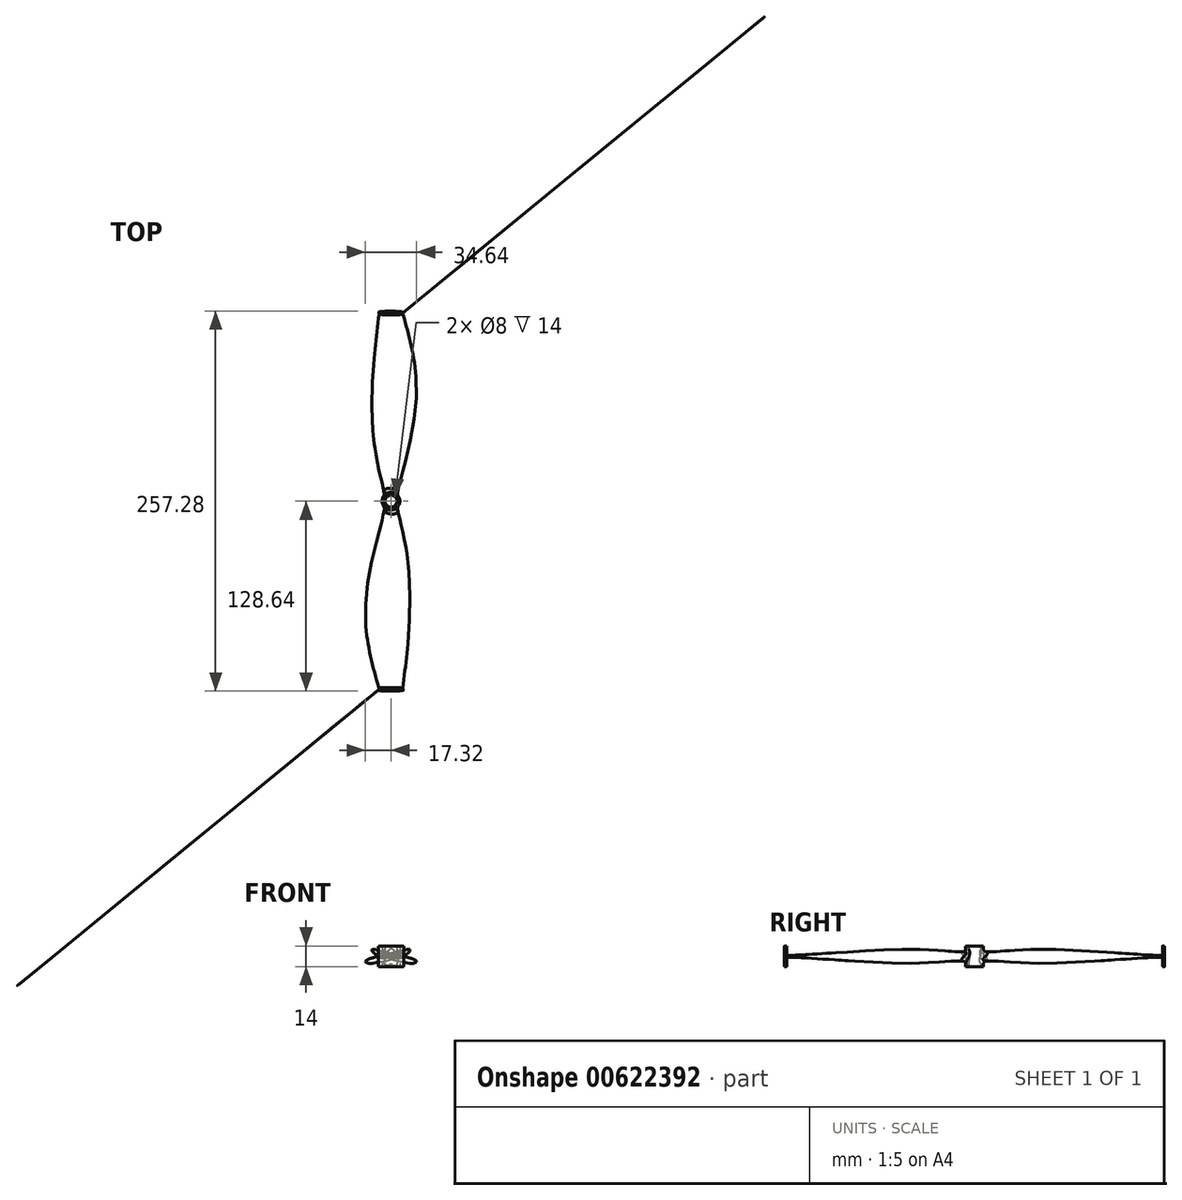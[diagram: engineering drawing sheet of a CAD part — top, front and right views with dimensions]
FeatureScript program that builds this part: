
annotation { "Feature Type Name" : "Feature", "Feature Type Description" : "" }
export const myFeature = defineFeature(function(context is Context, id is Id, definition is map)
    precondition{}
    {
        {
            var Q0;
            Q0=qCreatedBy(makeId("Top.planeOp"),FACE);
            var sketch = newSketch(context, id + "F0", { "sketchPlane" : qUnion([Q0])});
            skCircle(sketch, "E0", {"center": v(0, 0) * mm, "radius": 6 * mm});
            skCircle(sketch, "E1.0", {"center": v(0, 0) * mm, "radius": 4 * mm});
            skSolve(sketch);
        }
        {
            var Q0;
            Q0=qCreatedBy(makeId("Front.planeOp"),FACE);
            cPlane(context, id + "F1", {"entities" : qUnion([Q0]), "cplaneType" : CPlaneType.OFFSET, "offset" : 2 * mm, "width" : 150 * mm, "height" : 150 * mm});
        }
        {
            var Q0;
            Q0=qCreatedBy(makeId("Front.planeOp"),FACE);
            cPlane(context, id + "F2", {"entities" : qUnion([Q0]), "cplaneType" : CPlaneType.OFFSET, "offset" : 18 * mm, "width" : 150 * mm, "height" : 150 * mm});
        }
        {
            var Q0;
            Q0=qCreatedBy(makeId("Front.planeOp"),FACE);
            cPlane(context, id + "F3", {"entities" : qUnion([Q0]), "cplaneType" : CPlaneType.OFFSET, "offset" : 84 * mm, "width" : 150 * mm, "height" : 150 * mm});
        }
        {
            var Q0;
            Q0=qCreatedBy(makeId("Front.planeOp"),FACE);
            cPlane(context, id + "F4", {"entities" : qUnion([Q0]), "cplaneType" : CPlaneType.OFFSET, "offset" : 128 * mm, "width" : 150 * mm, "height" : 150 * mm});
        }
        {
            var Q0;
            Q0=qCreatedBy(id+"F1.planeOp",FACE);
            var sketch = newSketch(context, id + "F5", { "sketchPlane" : qUnion([Q0])});
            skLineSegment(sketch, "E2", {"start": v(-9.97, 0) * mm, "end": v(8.52, 0) * mm, "construction": true});
            skLineSegment(sketch, "E3", {"start": v(5.45, 4.57) * mm, "end": v(0, 0) * mm, "construction": true});
            skLineSegment(sketch, "E4", {"start": v(0, 0) * mm, "end": v(4.94, -5.88) * mm, "construction": true});
            skEllipse(sketch, "E5", {"center": v(0, 0) * mm, "majorRadius": 5 * mm, "minorRadius": 2 * mm, "majorAxis": v(0.76, 0.64)});
            skSolve(sketch);
        }
        {
            var Q0;
            Q0=qCreatedBy(id+"F2.planeOp",FACE);
            var sketch = newSketch(context, id + "F6", { "sketchPlane" : qUnion([Q0])});
            skLineSegment(sketch, "E6", {"start": v(-11.2, 0) * mm, "end": v(9.29, 0) * mm, "construction": true});
            skLineSegment(sketch, "E7", {"start": v(9.29, 0) * mm, "end": v(0, 0) * mm, "construction": true});
            skLineSegment(sketch, "E8", {"start": v(0, 0) * mm, "end": v(2.83, -6.16) * mm, "construction": true});
            skLineSegment(sketch, "E9", {"start": v(0, 0) * mm, "end": v(8.55, 3.92) * mm, "construction": true});
            skEllipse(sketch, "E10", {"center": v(0, 0) * mm, "majorRadius": 8 * mm, "minorRadius": 1.43 * mm, "majorAxis": v(0.92, 0.4)});
            skSolve(sketch);
        }
        {
            var Q0;
            Q0=qCreatedBy(id+"F3.planeOp",FACE);
            var sketch = newSketch(context, id + "F7", { "sketchPlane" : qUnion([Q0])});
            skEllipse(sketch, "E11", {"center": v(-2.33, 0) * mm, "majorRadius": 15 * mm, "minorRadius": 0.74 * mm, "majorAxis": v(0.98, 0.2)});
            skSolve(sketch);
        }
        {
            var Q0;
            Q0=qCreatedBy(id+"F4.planeOp",FACE);
            var sketch = newSketch(context, id + "F8", { "sketchPlane" : qUnion([Q0])});
            skEllipse(sketch, "E12", {"center": v(0, 0) * mm, "majorRadius": 7.81 * mm, "minorRadius": 0.53 * mm, "majorAxis": v(1, 0)});
            skSolve(sketch);
        }
        {
            var Q0;
            Q0=qCreatedBy(makeId("Front.planeOp"),FACE);
            var sketch = newSketch(context, id + "F9", { "sketchPlane" : qUnion([Q0])});
            skLineSegment(sketch, "E13", {"start": v(0, -14) * mm, "end": v(0, 19.94) * mm, "construction": true});
            skLineSegment(sketch, "E14", {"start": v(23.62, 0) * mm, "end": v(-25.85, 0) * mm, "construction": true});
            skSolve(sketch);
        }
        {
            var Q0;
            Q0=makeQuery(id+"F0.imprint","IMPRINT",FACE,{"disambiguationData":[TD([[makeQuery(id+"F0.imprint","IMPRINT",EDGE,{"derivedFrom":sQuery(id+"F0.wireOp",EDGE,"E0")}),1.0]])]});
            var Q1;
            Q1=makeQuery(id+"F0.imprint","IMPRINT",FACE,{"disambiguationData":[TD([[makeQuery(id+"F0.imprint","IMPRINT",EDGE,{"derivedFrom":sQuery(id+"F0.wireOp",EDGE,"E1.0")}),1.0]])]});
            extrude(context, id + "F10", {"entities" : qUnion([Q0, Q1]), "depth" : 14 * mm, "offsetDistance" : 25 * mm, "symmetric" : true});
        }
        {
            var Q1;
            Q1 = qSketchRegion(id + "F5", true);
            var Q2;
            Q2 = qSketchRegion(id + "F6", true);
            var Q3;
            Q3 = qSketchRegion(id + "F7", true);
            var Q4;
            Q4 = qSketchRegion(id + "F8", true);
            loft(context, id + "F11", {"operationType" : NewBodyOperationType.ADD, "sheetProfilesArray" : [{ "sheetProfileEntities" : qUnion([Q1]) }, { "sheetProfileEntities" : qUnion([Q2]) }, { "sheetProfileEntities" : qUnion([Q3]) }, { "sheetProfileEntities" : qUnion([Q4]) }]});
        }
        {
            var Q0;
            Q0=makeQuery(id+"F0.imprint","IMPRINT",FACE,{"disambiguationData":[TD([[makeQuery(id+"F0.imprint","IMPRINT",EDGE,{"derivedFrom":sQuery(id+"F0.wireOp",EDGE,"E1.0")}),1.0]])]});
            extrude(context, id + "F12", {"entities" : qUnion([Q0]), "operationType" : NewBodyOperationType.REMOVE, "depth" : 25 * mm, "offsetDistance" : 25 * mm, "symmetric" : true});
        }
        {
            var Q0;
            Q0=makeQuery(id+"F11.boolean.opBoolean","INTERSECT",EDGE,{"derivedFrom":[makeQuery(id+"F10.opExtrude","SWEPT_FACE",FACE,{"disambiguationData":[OSD([sQuery(id+"F0.wireOp",EDGE,"E0")])]}),makeQuery(id+"F11.opLoft","SWEPT_FACE",FACE,{"disambiguationData":[OSD([sQuery(id+"F5.wireOp",EDGE,"E5"),sQuery(id+"F6.wireOp",EDGE,"E10")])]})]});
            fillet(context, id + "F13", {"entities" : qUnion([Q0]), "radius" : 3 * mm, "tangentPropagation" : true, "allowEdgeOverflow" : false});
        }
        {
            var Q0;
            Q0=qCreatedBy(makeId("Top.planeOp"),FACE);
            var sketch = newSketch(context, id + "F14", { "sketchPlane" : qUnion([Q0])});
            skEllipse(sketch, "E15", {"center": v(0, -127.88) * mm, "majorRadius": 8.54 * mm, "minorRadius": 0.75 * mm, "majorAxis": v(1, 0)});
            skSolve(sketch);
        }
        {
            var Q0;
            Q0=makeQuery(id+"F14.imprint","IMPRINT",FACE,{"disambiguationData":[TD([[makeQuery(id+"F14.imprint","IMPRINT",EDGE,{"derivedFrom":sQuery(id+"F14.wireOp",EDGE,"E15")}),1.0]])]});
            extrude(context, id + "F15", {"entities" : qUnion([Q0]), "operationType" : NewBodyOperationType.ADD, "depth" : 14 * mm, "offsetDistance" : 25 * mm, "hasSecondDirection" : true, "secondDirectionOppositeDirection" : true, "secondDirectionDepth" : 0.5 * mm, "symmetric" : true});
        }
        {
            var Q0;
            Q0=makeQuery(id+"F15.boolean.opBoolean","INTERSECT",EDGE,{"derivedFrom":[makeQuery(id+"F11.opLoft","SWEPT_FACE",FACE,{"disambiguationData":[OSD([sQuery(id+"F5.wireOp",EDGE,"E5"),sQuery(id+"F6.wireOp",EDGE,"E10")])]}),makeQuery(id+"F15.opExtrude","SWEPT_FACE",FACE,{"disambiguationData":[OSD([sQuery(id+"F14.wireOp",EDGE,"E15")])]})]});
            fillet(context, id + "F16", {"entities" : qUnion([Q0]), "radius" : 1 * mm, "tangentPropagation" : true, "allowEdgeOverflow" : false});
        }
        {
            var Q0;
            Q0=makeQuery(id+"F10.opExtrude","SWEPT_BODY",BODY,{"disambiguationData":[OSD([sQuery(id+"F0.wireOp",EDGE,"E0")])]});
            var Q1;
            Q1=sQuery(id+"F9.wireOp",EDGE,"E13");
            transform(context, id + "F17", {"entities" : qUnion([Q0]), "transformType" : TransformType.ROTATION, "transformAxis" : qUnion([Q1]), "angle" : 180 * degree, "makeCopy" : true});
        }
    });
